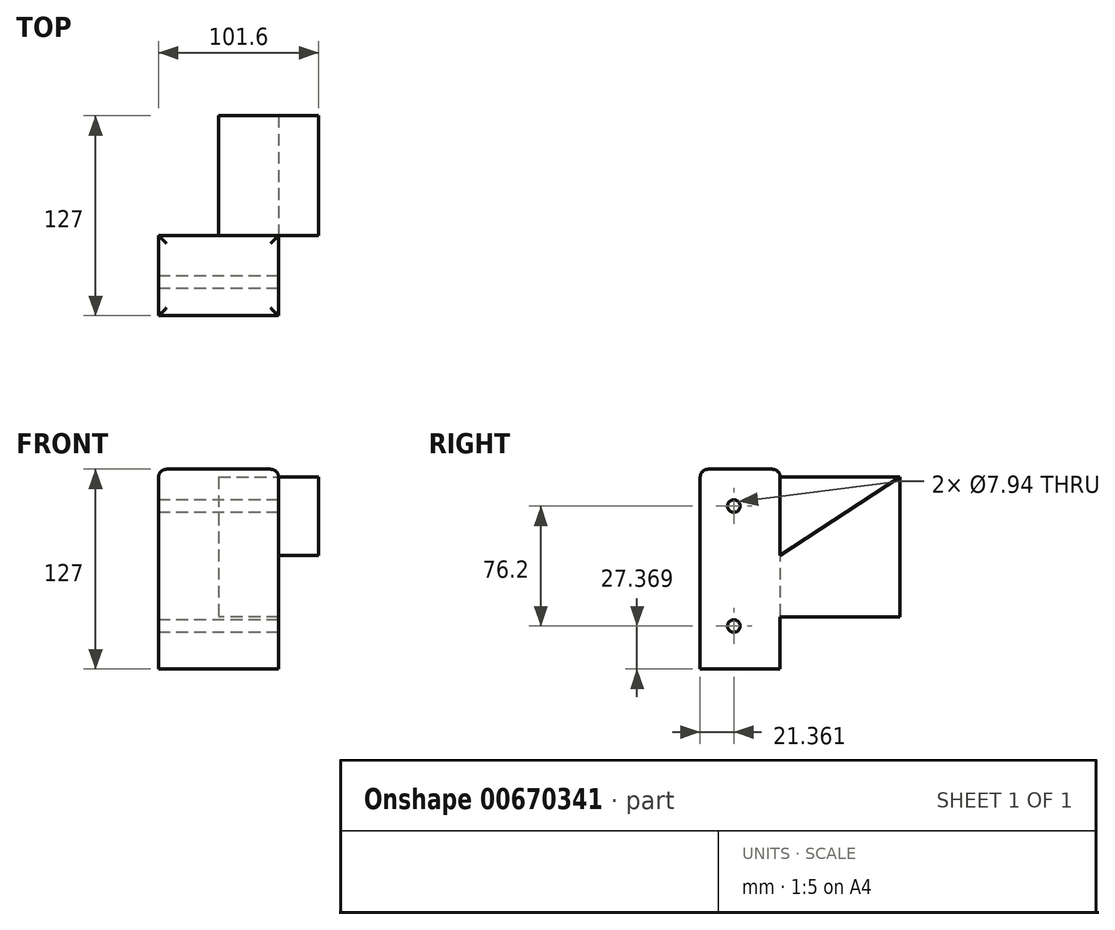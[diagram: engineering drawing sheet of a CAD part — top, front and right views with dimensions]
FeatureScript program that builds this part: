
annotation { "Feature Type Name" : "Feature", "Feature Type Description" : "" }
export const myFeature = defineFeature(function(context is Context, id is Id, definition is map)
    precondition{}
    {
        {
            var Q0;
            Q0=qCreatedBy(makeId("Top.planeOp"),FACE);
            var sketch = newSketch(context, id + "F0", { "sketchPlane" : qUnion([Q0])});
            skLineSegment(sketch, "E0.bottom", {"start": v(0, 0) * mm, "end": v(76.2, 0) * mm});
            skLineSegment(sketch, "E0.top", {"start": v(0, 50.8) * mm, "end": v(76.2, 50.8) * mm});
            skLineSegment(sketch, "E0.left", {"start": v(0, 0) * mm, "end": v(0, 50.8) * mm});
            skLineSegment(sketch, "E0.right", {"start": v(76.2, 0) * mm, "end": v(76.2, 50.8) * mm});
            skSolve(sketch);
        }
        {
            var Q0;
            Q0=makeQuery(id+"F0.imprint","IMPRINT",FACE,{"disambiguationData":[TD([[makeQuery(id+"F0.imprint","IMPRINT",EDGE,{"derivedFrom":sQuery(id+"F0.wireOp",EDGE,"E0.bottom")}),1.0]])]});
            extrude(context, id + "F1", {"entities" : qUnion([Q0]), "depth" : 127 * mm, "offsetDistance" : 25.4 * mm});
        }
        {
            var Q0;
            Q0=makeQuery(id+"F1.opExtrude","CAP_FACE",FACE,{"disambiguationData":[OSD([sQuery(id+"F0.wireOp",EDGE,"E0.bottom"),sQuery(id+"F0.wireOp",EDGE,"E0.top"),sQuery(id+"F0.wireOp",EDGE,"E0.left"),sQuery(id+"F0.wireOp",EDGE,"E0.right")])],"isStart":false});
            fillet(context, id + "F2", {"entities" : qUnion([Q0]), "radius" : 5.08 * mm, "tangentPropagation" : true, "allowEdgeOverflow" : false});
        }
        {
            var Q0;
            Q0=makeQuery(id+"F1.opExtrude","SWEPT_FACE",FACE,{"disambiguationData":[OSD([sQuery(id+"F0.wireOp",EDGE,"E0.left")])]});
            var sketch = newSketch(context, id + "F3", { "sketchPlane" : qUnion([Q0])});
            skLineSegment(sketch, "E1", {"start": v(-21.36, 103.57) * mm, "end": v(-21.36, 27.37) * mm});
            skSolve(sketch);
        }
        {
            var Q0;
            Q0=sQuery(id+"F3.wireOp",VERTEX,"E1.start");
            var Q1;
            Q1=sQuery(id+"F3.wireOp",VERTEX,"E1.end");
            var Q2;
            Q2=makeQuery(id+"F1.opExtrude","SWEPT_BODY",BODY,{"disambiguationData":[OSD([sQuery(id+"F0.wireOp",EDGE,"E0.bottom"),sQuery(id+"F0.wireOp",EDGE,"E0.top"),sQuery(id+"F0.wireOp",EDGE,"E0.left"),sQuery(id+"F0.wireOp",EDGE,"E0.right")])]});
            hole(context, id + "F4", {"style" : HoleStyle.SIMPLE, "endStyle" : HoleEndStyle.THROUGH, "standardTappedOrClearance" : lookupTablePath({ "standard" : "ANSI", "engagement" : "75%", "pitch" : "16 tpi", "size" : "3/8", "type" : "Tapped" }), "standardBlindInLast" : lookupTablePath({ "standard" : "ANSI", "engagement" : "75%", "pitch" : "16 tpi", "size" : "3/8", "type" : "Tapped" }), "holeDiameter" : 7.94 * mm, "majorDiameter" : 9.52 * mm, "showTappedDepth" : true, "tappedDepth" : 38.1 * mm, "tapClearance" : 3, "locations" : qUnion([Q0, Q1]), "scope" : qUnion([Q2])});
        }
        {
            var Q0;
            Q0=makeQuery(id+"F1.opExtrude","SWEPT_FACE",FACE,{"disambiguationData":[OSD([sQuery(id+"F0.wireOp",EDGE,"E0.top")])]});
            var sketch = newSketch(context, id + "F5", { "sketchPlane" : qUnion([Q0])});
            skPoint(sketch, "E2.oppositeSnap0", {"position": v(-38.1, 121.92) * mm});
            skLineSegment(sketch, "E2.bottom", {"start": v(-76.2, 121.92) * mm, "end": v(-38.1, 121.92) * mm});
            skLineSegment(sketch, "E2.top", {"start": v(-76.2, 33.02) * mm, "end": v(-38.1, 33.02) * mm});
            skLineSegment(sketch, "E2.left", {"start": v(-76.2, 121.92) * mm, "end": v(-76.2, 33.02) * mm});
            skLineSegment(sketch, "E2.right", {"start": v(-38.1, 121.92) * mm, "end": v(-38.1, 33.02) * mm});
            skSolve(sketch);
        }
        {
            var Q0;
            Q0=makeQuery(id+"F5.imprint","IMPRINT",FACE,{"disambiguationData":[TD([[makeQuery(id+"F5.imprint","IMPRINT",EDGE,{"derivedFrom":sQuery(id+"F5.wireOp",EDGE,"E2.bottom")}),1.0]])]});
            extrude(context, id + "F6", {"entities" : qUnion([Q0]), "operationType" : NewBodyOperationType.ADD, "depth" : 76.2 * mm, "offsetDistance" : 25.4 * mm});
        }
        {
            var Q0;
            Q0=makeQuery(id+"F6.boolean.opBoolean","MERGE",FACE,{"derivedFrom":[makeQuery(id+"F1.opExtrude","SWEPT_FACE",FACE,{"disambiguationData":[OSD([sQuery(id+"F0.wireOp",EDGE,"E0.right")])]}),makeQuery(id+"F6.opExtrude","SWEPT_FACE",FACE,{"disambiguationData":[OSD([sQuery(id+"F5.wireOp",EDGE,"E2.left")])]})]});
            var sketch = newSketch(context, id + "F7", { "sketchPlane" : qUnion([Q0])});
            skLineSegment(sketch, "E3", {"start": v(50.8, 121.92) * mm, "end": v(50.8, 72.31) * mm});
            skLineSegment(sketch, "E4", {"start": v(50.8, 72.31) * mm, "end": v(127, 121.92) * mm});
            skLineSegment(sketch, "E5", {"start": v(127, 121.92) * mm, "end": v(50.8, 121.92) * mm});
            skSolve(sketch);
        }
        {
            var Q0;
            Q0=makeQuery(id+"F7.imprint","IMPRINT",FACE,{"disambiguationData":[TD([[makeQuery(id+"F7.imprint","IMPRINT",EDGE,{"derivedFrom":sQuery(id+"F7.wireOp",EDGE,"E3")}),1.0]])]});
            extrude(context, id + "F8", {"entities" : qUnion([Q0]), "operationType" : NewBodyOperationType.ADD, "depth" : 25.4 * mm, "offsetDistance" : 25.4 * mm});
        }
    });
